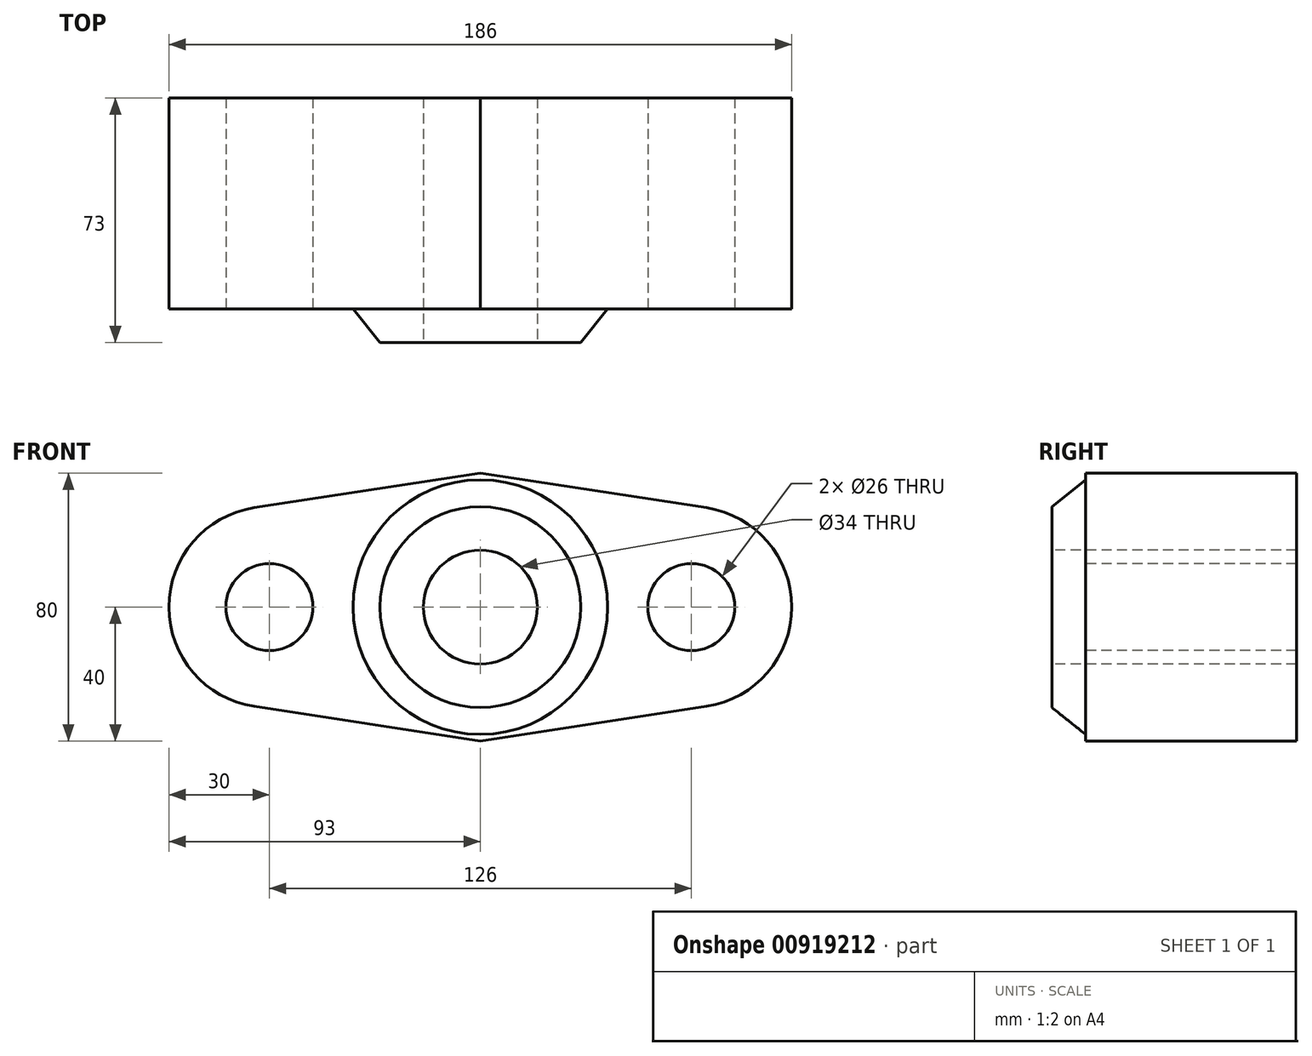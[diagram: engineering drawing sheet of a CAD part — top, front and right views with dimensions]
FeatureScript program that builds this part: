
annotation { "Feature Type Name" : "Feature", "Feature Type Description" : "" }
export const myFeature = defineFeature(function(context is Context, id is Id, definition is map)
    precondition{}
    {
        {
            var Q0;
            Q0=qCreatedBy(makeId("Front.planeOp"),FACE);
            var sketch = newSketch(context, id + "F0", { "sketchPlane" : qUnion([Q0])});
            skLineSegment(sketch, "E0", {"start": v(-196.82, 0) * mm, "end": v(212.7, 0) * mm, "construction": true});
            skLineSegment(sketch, "E1", {"start": v(0, 82.02) * mm, "end": v(0, -85.36) * mm, "construction": true});
            skLineSegment(sketch, "E2.0", {"start": v(-63, 82.02) * mm, "end": v(-63, -85.36) * mm, "construction": true});
            skLineSegment(sketch, "E3.0", {"start": v(63, 82.02) * mm, "end": v(63, -85.36) * mm, "construction": true});
            skCircle(sketch, "E4", {"center": v(-63, 0) * mm, "radius": 13 * mm});
            skCircle(sketch, "E5", {"center": v(63, 0) * mm, "radius": 13 * mm});
            skLineSegment(sketch, "E6", {"start": v(0, 40) * mm, "end": v(67.54, 29.65) * mm});
            skLineSegment(sketch, "E7", {"start": v(0, 40) * mm, "end": v(-67.54, 29.65) * mm});
            skLineSegment(sketch, "E8", {"start": v(0, -40) * mm, "end": v(-67.54, -29.65) * mm});
            skLineSegment(sketch, "E9", {"start": v(67.54, -29.65) * mm, "end": v(67.54, -29.65) * mm});
            skArc(sketch, "E10", {"start": v(-67.54, 29.65) * mm, "mid": v(-93, 0) * mm, "end": v(-67.54, -29.65) * mm});
            skLineSegment(sketch, "E11", {"start": v(-72.76, -28.85) * mm, "end": v(-72.78, -28.85) * mm});
            skLineSegment(sketch, "E12", {"start": v(-67.54, -29.65) * mm, "end": v(-72.76, -28.85) * mm});
            skArc(sketch, "E13", {"start": v(67.54, -29.65) * mm, "mid": v(67.55, -29.65) * mm, "end": v(67.57, -29.65) * mm});
            skLineSegment(sketch, "E14", {"start": v(75.08, -28.5) * mm, "end": v(75.14, -28.5) * mm});
            skArc(sketch, "E15", {"start": v(67.57, -29.65) * mm, "mid": v(93, 0.01) * mm, "end": v(67.54, 29.65) * mm});
            skLineSegment(sketch, "E16", {"start": v(75.08, -28.5) * mm, "end": v(75.08, -28.5) * mm});
            skLineSegment(sketch, "E17", {"start": v(0, -40) * mm, "end": v(67.57, -29.65) * mm});
            skCircle(sketch, "E18", {"center": v(0, 0) * mm, "radius": 38 * mm});
            skSolve(sketch);
        }
        {
            var Q0;
            Q0=makeQuery(id+"F0.imprint","IMPRINT",FACE,{"disambiguationData":[TD([[makeQuery(id+"F0.imprint","IMPRINT",EDGE,{"derivedFrom":sQuery(id+"F0.wireOp",EDGE,"E4")}),-1.0]])]});
            var Q1;
            Q1=makeQuery(id+"F0.imprint","IMPRINT",FACE,{"disambiguationData":[TD([[makeQuery(id+"F0.imprint","IMPRINT",EDGE,{"derivedFrom":sQuery(id+"F0.wireOp",EDGE,"E4")}),1.0]])]});
            var Q2;
            Q2=makeQuery(id+"F0.imprint","IMPRINT",FACE,{"disambiguationData":[TD([[makeQuery(id+"F0.imprint","IMPRINT",EDGE,{"derivedFrom":sQuery(id+"F0.wireOp",EDGE,"E18")}),1.0]])]});
            var Q3;
            Q3=makeQuery(id+"F0.imprint","IMPRINT",FACE,{"disambiguationData":[TD([[makeQuery(id+"F0.imprint","IMPRINT",EDGE,{"derivedFrom":sQuery(id+"F0.wireOp",EDGE,"E5")}),1.0]])]});
            extrude(context, id + "F1", {"entities" : qUnion([Q0, Q1, Q2, Q3]), "oppositeDirection" : true, "depth" : 28 * mm, "offsetDistance" : 25 * mm});
        }
        {
            var Q0;
            Q0=makeQuery(id+"F0.imprint","IMPRINT",FACE,{"disambiguationData":[TD([[makeQuery(id+"F0.imprint","IMPRINT",EDGE,{"derivedFrom":sQuery(id+"F0.wireOp",EDGE,"E18")}),1.0]])]});
            cPlane(context, id + "F2", {"entities" : qUnion([Q0]), "cplaneType" : CPlaneType.OFFSET, "offset" : 10 * mm, "width" : 150 * mm, "height" : 150 * mm});
        }
        {
            var Q0;
            Q0=qCreatedBy(id+"F2.planeOp",FACE);
            var sketch = newSketch(context, id + "F3", { "sketchPlane" : qUnion([Q0])});
            skCircle(sketch, "E19", {"center": v(0, 0) * mm, "radius": 30 * mm});
            skSolve(sketch);
        }
        {
            var Q1;
            Q1=makeQuery(id+"F3.imprint","IMPRINT",FACE,{"disambiguationData":[TD([[makeQuery(id+"F3.imprint","IMPRINT",EDGE,{"derivedFrom":sQuery(id+"F3.wireOp",EDGE,"E19")}),1.0]])]});
            var Q2;
            Q2=makeQuery(id+"F0.imprint","IMPRINT",FACE,{"disambiguationData":[TD([[makeQuery(id+"F0.imprint","IMPRINT",EDGE,{"derivedFrom":sQuery(id+"F0.wireOp",EDGE,"E18")}),1.0]])]});
            loft(context, id + "F4", {"operationType" : NewBodyOperationType.ADD, "sheetProfilesArray" : [{ "sheetProfileEntities" : qUnion([Q1]) }, { "sheetProfileEntities" : qUnion([Q2]) }]});
        }
        {
            var Q0;
            Q0=sQuery(id+"F0.wireOp",VERTEX,"E4.center");
            var Q1;
            Q1=makeQuery(id+"F1.opExtrude","SWEPT_BODY",BODY,{"disambiguationData":[OSD([sQuery(id+"F0.wireOp",EDGE,"E6"),sQuery(id+"F0.wireOp",EDGE,"E7"),sQuery(id+"F0.wireOp",EDGE,"E8"),sQuery(id+"F0.wireOp",EDGE,"E10"),sQuery(id+"F0.wireOp",EDGE,"E15"),sQuery(id+"F0.wireOp",EDGE,"E17")])]});
            hole(context, id + "F5", {"style" : HoleStyle.SIMPLE, "endStyle" : HoleEndStyle.THROUGH, "holeDiameter" : 26 * mm, "majorDiameter" : 5 * mm, "isTappedThrough" : true, "tappedDepth" : 12 * mm, "tapClearance" : 3, "locations" : qUnion([Q0]), "scope" : qUnion([Q1])});
        }
        {
            var Q0;
            Q0=sQuery(id+"F0.wireOp",VERTEX,"E5.center");
            var Q1;
            Q1=makeQuery(id+"F1.opExtrude","SWEPT_BODY",BODY,{"disambiguationData":[OSD([sQuery(id+"F0.wireOp",EDGE,"E6"),sQuery(id+"F0.wireOp",EDGE,"E7"),sQuery(id+"F0.wireOp",EDGE,"E8"),sQuery(id+"F0.wireOp",EDGE,"E10"),sQuery(id+"F0.wireOp",EDGE,"E15"),sQuery(id+"F0.wireOp",EDGE,"E17")])]});
            hole(context, id + "F6", {"style" : HoleStyle.SIMPLE, "endStyle" : HoleEndStyle.THROUGH, "holeDiameter" : 26 * mm, "majorDiameter" : 5 * mm, "isTappedThrough" : true, "tappedDepth" : 12 * mm, "tapClearance" : 3, "locations" : qUnion([Q0]), "scope" : qUnion([Q1])});
        }
        {
            var Q0;
            Q0=sQuery(id+"F0.wireOp",VERTEX,"E18.center");
            var Q1;
            Q1=makeQuery(id+"F1.opExtrude","SWEPT_BODY",BODY,{"disambiguationData":[OSD([sQuery(id+"F0.wireOp",EDGE,"E6"),sQuery(id+"F0.wireOp",EDGE,"E7"),sQuery(id+"F0.wireOp",EDGE,"E8"),sQuery(id+"F0.wireOp",EDGE,"E10"),sQuery(id+"F0.wireOp",EDGE,"E15"),sQuery(id+"F0.wireOp",EDGE,"E17")])]});
            hole(context, id + "F7", {"style" : HoleStyle.SIMPLE, "endStyle" : HoleEndStyle.THROUGH, "holeDiameter" : 34 * mm, "majorDiameter" : 5 * mm, "isTappedThrough" : true, "tappedDepth" : 12 * mm, "tapClearance" : 3, "locations" : qUnion([Q0]), "scope" : qUnion([Q1])});
        }
        {
            var Q0;
            Q0=makeQuery(id+"F4.opLoft","CAP_FACE",FACE,{"disambiguationData":[OSD([makeQuery(id+"F3.imprint","IMPRINT",FACE,{"disambiguationData":[TD([[makeQuery(id+"F3.imprint","IMPRINT",EDGE,{"derivedFrom":sQuery(id+"F3.wireOp",EDGE,"E19")}),1.0]])]})])],"isStart":true});
            var sketch = newSketch(context, id + "F8", { "sketchPlane" : qUnion([Q0])});
            skCircle(sketch, "E20", {"center": v(0, 0) * mm, "radius": 17 * mm});
            skSolve(sketch);
        }
        {
            var Q0;
            Q0=makeQuery(id+"F8.imprint","IMPRINT",FACE,{"disambiguationData":[TD([[makeQuery(id+"F8.imprint","IMPRINT",EDGE,{"derivedFrom":sQuery(id+"F8.wireOp",EDGE,"E20")}),1.0]])]});
            extrude(context, id + "F9", {"entities" : qUnion([Q0]), "operationType" : NewBodyOperationType.REMOVE, "oppositeDirection" : true, "depth" : 25 * mm, "offsetDistance" : 25 * mm});
        }
        {
            var Q0;
            Q0=makeQuery(id+"F1.opExtrude","CAP_FACE",FACE,{"disambiguationData":[OSD([sQuery(id+"F0.wireOp",EDGE,"E6"),sQuery(id+"F0.wireOp",EDGE,"E7"),sQuery(id+"F0.wireOp",EDGE,"E8"),sQuery(id+"F0.wireOp",EDGE,"E10"),sQuery(id+"F0.wireOp",EDGE,"E15"),sQuery(id+"F0.wireOp",EDGE,"E17")])],"isStart":false});
            extrude(context, id + "F10", {"entities" : qUnion([Q0]), "operationType" : NewBodyOperationType.ADD, "depth" : 35 * mm, "offsetDistance" : 25 * mm});
        }
    });
